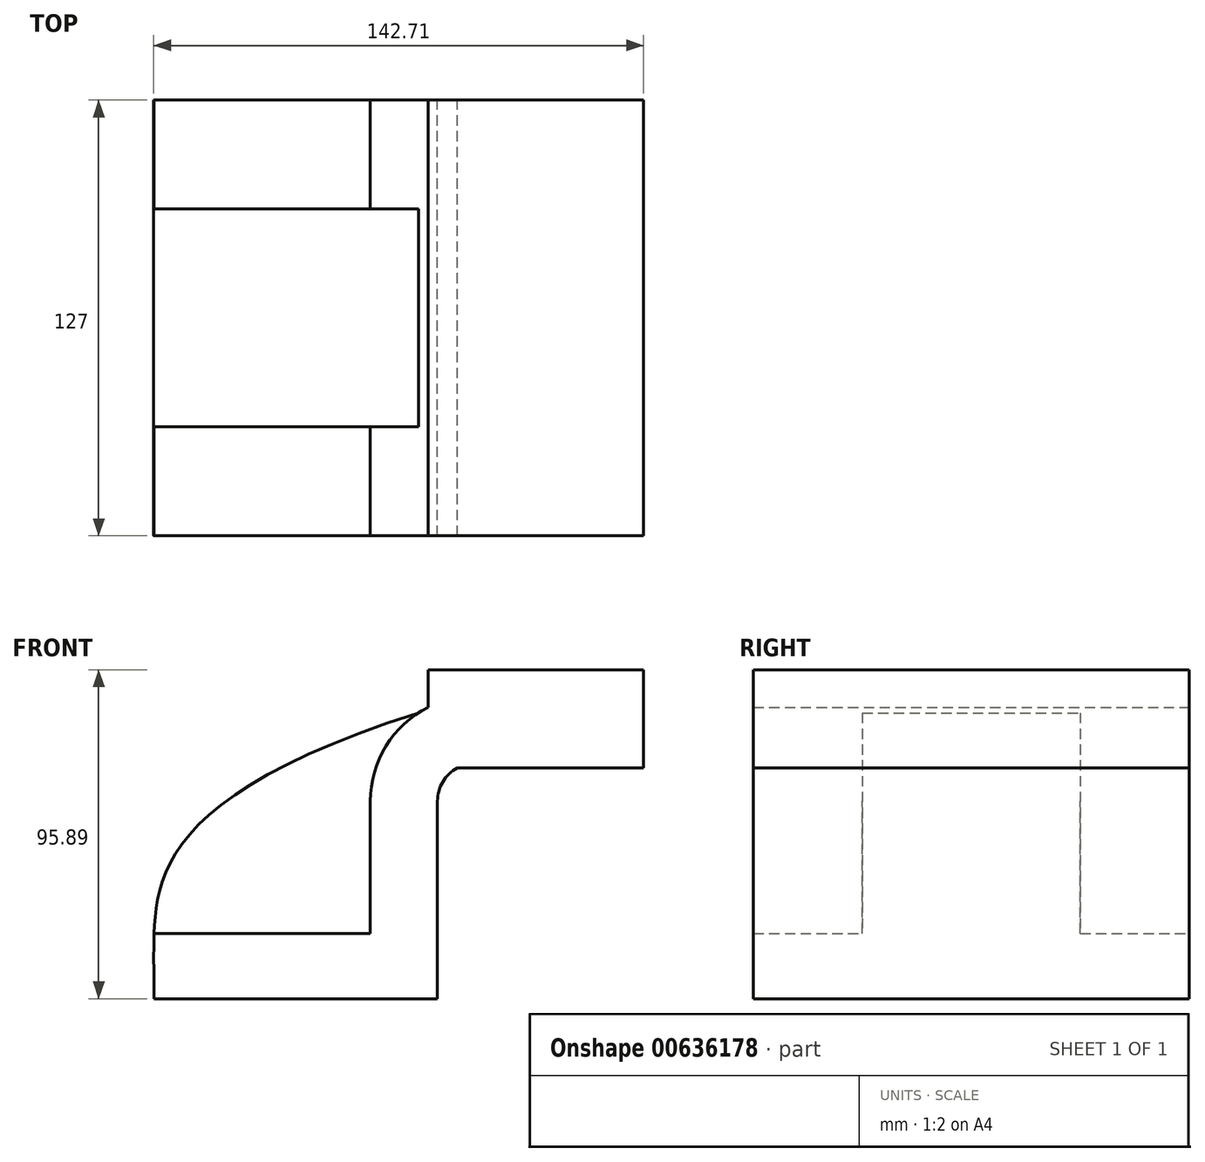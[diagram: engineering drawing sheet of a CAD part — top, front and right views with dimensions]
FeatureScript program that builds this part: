
annotation { "Feature Type Name" : "Feature", "Feature Type Description" : "" }
export const myFeature = defineFeature(function(context is Context, id is Id, definition is map)
    precondition{}
    {
        {
            var Q0;
            Q0=qCreatedBy(makeId("Front.planeOp"),FACE);
            var sketch = newSketch(context, id + "F0", { "sketchPlane" : qUnion([Q0])});
            skLineSegment(sketch, "E0.bottom", {"start": v(-41.28, 9.53) * mm, "end": v(41.28, 9.53) * mm});
            skLineSegment(sketch, "E0.top", {"start": v(-41.28, -9.53) * mm, "end": v(41.28, -9.53) * mm});
            skLineSegment(sketch, "E0.left", {"start": v(-41.28, 9.53) * mm, "end": v(-41.28, -9.53) * mm});
            skLineSegment(sketch, "E0.right", {"start": v(41.28, 9.53) * mm, "end": v(41.28, -9.53) * mm});
            skPoint(sketch, "E0.middle", {"position": v(0, 0) * mm});
            skLineSegment(sketch, "E1.bottom", {"start": v(38.55, 57.76) * mm, "end": v(101.3, 57.76) * mm});
            skLineSegment(sketch, "E1.top", {"start": v(38.55, 86.36) * mm, "end": v(101.3, 86.36) * mm});
            skLineSegment(sketch, "E1.left", {"start": v(38.55, 57.76) * mm, "end": v(38.55, 86.36) * mm});
            skLineSegment(sketch, "E1.right", {"start": v(101.3, 57.76) * mm, "end": v(101.3, 86.36) * mm});
            skPoint(sketch, "E1.middle", {"position": v(69.93, 72.06) * mm});
            skLineSegment(sketch, "E2", {"start": v(41.28, 9.53) * mm, "end": v(41.28, 48.02) * mm});
            skArc(sketch, "E3", {"start": v(41.28, 48.02) * mm, "mid": v(44.54, 55.9) * mm, "end": v(52.42, 59.16) * mm});
            skLineSegment(sketch, "E4", {"start": v(52.42, 59.16) * mm, "end": v(86.4, 59.16) * mm});
            skLineSegment(sketch, "E5.0", {"start": v(52.42, 78.72) * mm, "end": v(86.4, 78.72) * mm});
            skArc(sketch, "E5.1", {"start": v(21.72, 48.02) * mm, "mid": v(30.71, 69.73) * mm, "end": v(52.42, 78.72) * mm});
            skLineSegment(sketch, "E5.2", {"start": v(21.72, 9.53) * mm, "end": v(21.72, 48.02) * mm});
            skLineSegment(sketch, "E6", {"start": v(86.4, 59.16) * mm, "end": v(86.4, 86.36) * mm});
            skLineSegment(sketch, "E7", {"start": v(86.4, 86.36) * mm, "end": v(86.4, 57.76) * mm});
            skFitSpline(sketch, "E8", {"points": [v(52.42, 78.72) * mm, v(-41.28, 9.53) * mm, v(-41.28, -9.53) * mm], "startDerivative": vector(-373.5, -103.47) * mm, "endDerivative": vector(0, -47.7) * mm});
            skSolve(sketch);
        }
        {
            var Q0;
            {var subQ0=sQuery(id+"F0.wireOp",EDGE,"E0.left");Q0=makeQuery(id+"F0.imprint","IMPRINT",FACE,{"disambiguationData":[TD([[makeQuery(id+"F0.imprint","IMPRINT",EDGE,{"derivedFrom":subQ0}),-1.0]])]});}
            var Q1;
            {var subQ5=sQuery(id+"F0.wireOp",EDGE,"E4");Q1=makeQuery(id+"F0.imprint","IMPRINT",FACE,{"disambiguationData":[TD([[makeQuery(id+"F0.imprint","IMPRINT",EDGE,{"derivedFrom":subQ5}),-1.0]])]});}
            var Q2;
            {var subQ0=sQuery(id+"F0.wireOp",EDGE,"E5.1");var subQ1=sQuery(id+"F0.wireOp",EDGE,"E1.left");var subQ2=makeQuery(id+"F0.imprint","INTERSECT",VERTEX,{"derivedFrom":[subQ1,subQ0]});Q2=makeQuery(id+"F0.imprint","IMPRINT",FACE,{"disambiguationData":[TD([[makeQuery(id+"F0.imprint","IMPRINT",EDGE,{"disambiguationData":[TD([[subQ2,1.0]])],"derivedFrom":subQ1}),1.0]])]});}
            var Q3;
            Q3=makeQuery(id+"F0.imprint","IMPRINT",FACE,{"disambiguationData":[TD([[makeQuery(id+"F0.imprint","IMPRINT",EDGE,{"derivedFrom":sQuery(id+"F0.wireOp",EDGE,"E0.top")}),1.0]])]});
            var Q4;
            {var subQ4=sQuery(id+"F0.wireOp",EDGE,"E1.right");Q4=makeQuery(id+"F0.imprint","IMPRINT",FACE,{"disambiguationData":[TD([[makeQuery(id+"F0.imprint","IMPRINT",EDGE,{"derivedFrom":subQ4}),1.0]])]});}
            var Q5;
            {var subQ1=sQuery(id+"F0.wireOp",EDGE,"E5.0");Q5=makeQuery(id+"F0.imprint","IMPRINT",FACE,{"disambiguationData":[TD([[makeQuery(id+"F0.imprint","IMPRINT",EDGE,{"derivedFrom":subQ1}),1.0]])]});}
            var Q6;
            {var subQ0=sQuery(id+"F0.wireOp",EDGE,"E5.1");var subQ1=sQuery(id+"F0.wireOp",EDGE,"E1.left");var subQ2=makeQuery(id+"F0.imprint","INTERSECT",VERTEX,{"derivedFrom":[subQ1,subQ0]});Q6=makeQuery(id+"F0.imprint","IMPRINT",FACE,{"disambiguationData":[TD([[makeQuery(id+"F0.imprint","IMPRINT",EDGE,{"disambiguationData":[TD([[subQ2,1.0]])],"derivedFrom":subQ1}),-1.0]])]});}
            var Q7;
            {var subQ0=sQuery(id+"F0.wireOp",EDGE,"E2");Q7=makeQuery(id+"F0.imprint","IMPRINT",FACE,{"disambiguationData":[TD([[makeQuery(id+"F0.imprint","IMPRINT",EDGE,{"derivedFrom":subQ0}),1.0]])]});}
            var Q8;
            {var subQ0=sQuery(id+"F0.wireOp",EDGE,"E4");Q8=makeQuery(id+"F0.imprint","IMPRINT",FACE,{"disambiguationData":[TD([[makeQuery(id+"F0.imprint","IMPRINT",EDGE,{"derivedFrom":subQ0}),1.0]])]});}
            extrude(context, id + "F1", {"entities" : qUnion([Q0, Q1, Q2, Q3, Q4, Q5, Q6, Q7, Q8]), "endBound" : BoundingType.SYMMETRIC, "depth" : 127 * mm, "offsetDistance" : 25.4 * mm});
        }
        {
            var Q0;
            Q0 = qSketchRegion(id + "F0", true);
            extrude(context, id + "F2", {"entities" : qUnion([Q0]), "operationType" : NewBodyOperationType.ADD, "endBound" : BoundingType.SYMMETRIC, "depth" : 63.5 * mm, "offsetDistance" : 25.4 * mm});
        }
    });
